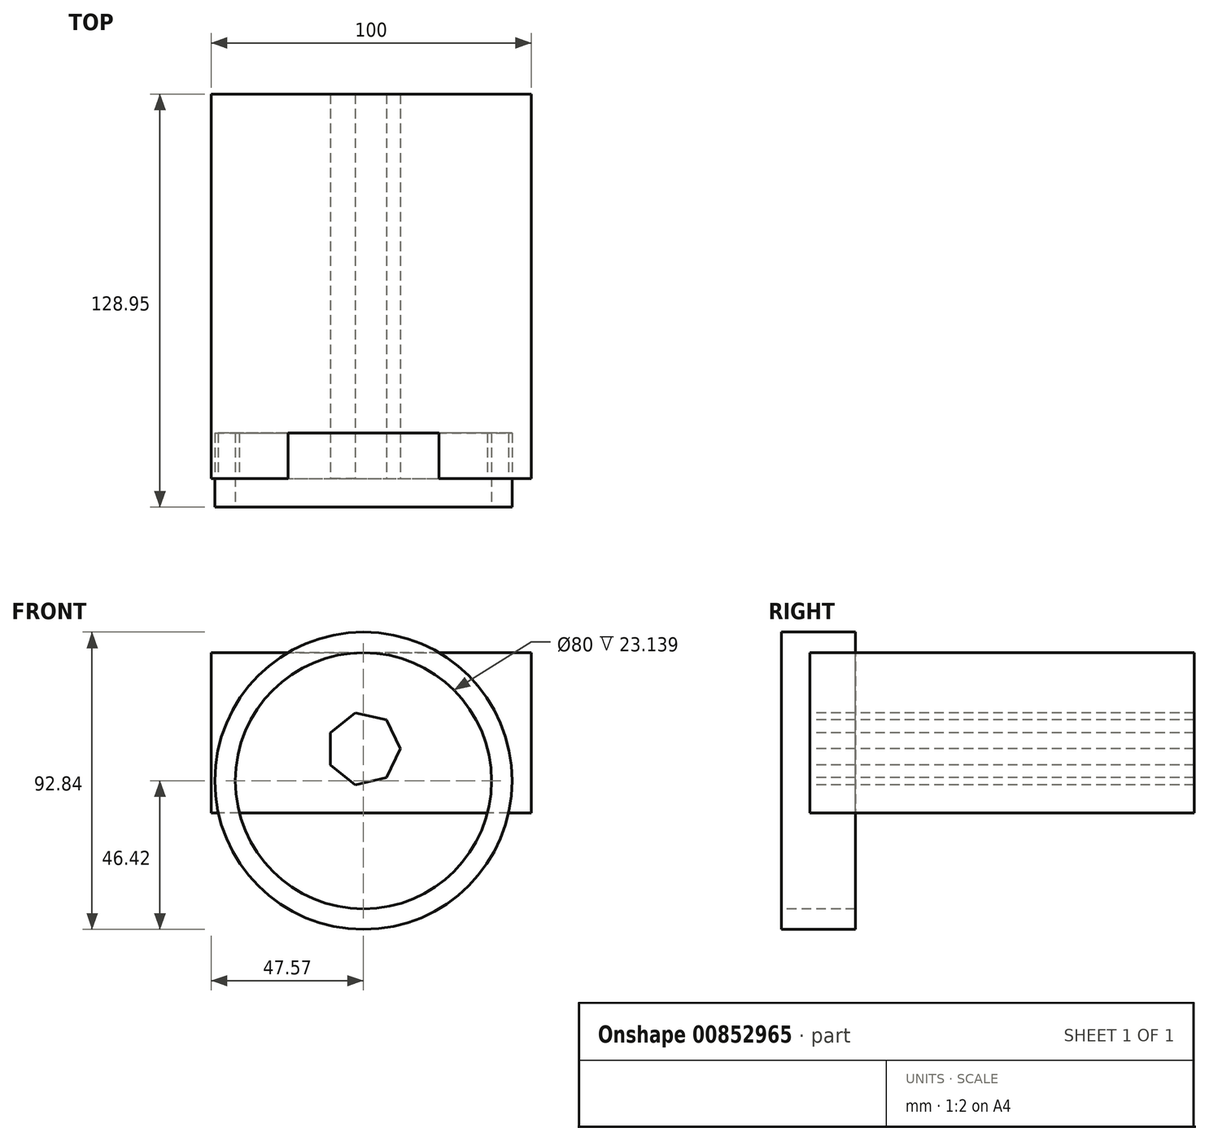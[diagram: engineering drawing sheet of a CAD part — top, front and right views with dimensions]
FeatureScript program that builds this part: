
annotation { "Feature Type Name" : "Feature", "Feature Type Description" : "" }
export const myFeature = defineFeature(function(context is Context, id is Id, definition is map)
    precondition{}
    {
        {
            var Q0;
            Q0=qCreatedBy(makeId("Top.planeOp"),FACE);
            var sketch = newSketch(context, id + "F0", { "sketchPlane" : qUnion([Q0])});
            skLineSegment(sketch, "E0.bottom", {"start": v(-47.57, 87.82) * mm, "end": v(52.43, 87.82) * mm});
            skLineSegment(sketch, "E0.top", {"start": v(-47.57, -32.18) * mm, "end": v(52.43, -32.18) * mm});
            skLineSegment(sketch, "E0.left", {"start": v(-47.57, 87.82) * mm, "end": v(-47.57, -32.18) * mm});
            skLineSegment(sketch, "E0.right", {"start": v(52.43, 87.82) * mm, "end": v(52.43, -32.18) * mm});
            skSolve(sketch);
        }
        {
            var Q0;
            Q0=makeQuery(id+"F0.imprint","IMPRINT",FACE,{"disambiguationData":[TD([[makeQuery(id+"F0.imprint","IMPRINT",EDGE,{"derivedFrom":sQuery(id+"F0.wireOp",EDGE,"E0.bottom")}),-1.0]])]});
            extrude(context, id + "F1", {"entities" : qUnion([Q0]), "depth" : 50 * mm, "offsetDistance" : 25 * mm});
        }
        {
            var Q0;
            Q0=makeQuery(id+"F1.opExtrude","SWEPT_FACE",FACE,{"disambiguationData":[OSD([sQuery(id+"F0.wireOp",EDGE,"E0.top")])]});
            var sketch = newSketch(context, id + "F2", { "sketchPlane" : qUnion([Q0])});
            skCircle(sketch, "E1.cCircle", {"center": v(0, 20) * mm, "radius": 10.38 * mm, "construction": true});
            skLineSegment(sketch, "E1.0", {"start": v(-2.56, 31.23) * mm, "end": v(7.18, 29) * mm});
            skLineSegment(sketch, "E1.1", {"start": v(7.18, 29) * mm, "end": v(11.52, 20) * mm});
            skLineSegment(sketch, "E1.2", {"start": v(11.52, 20) * mm, "end": v(7.18, 11) * mm});
            skLineSegment(sketch, "E1.3", {"start": v(7.18, 11) * mm, "end": v(-2.56, 8.77) * mm});
            skLineSegment(sketch, "E1.4", {"start": v(-2.56, 8.77) * mm, "end": v(-10.38, 15) * mm});
            skLineSegment(sketch, "E1.5", {"start": v(-10.38, 15) * mm, "end": v(-10.38, 25) * mm});
            skLineSegment(sketch, "E1.6", {"start": v(-10.38, 25) * mm, "end": v(-2.56, 31.23) * mm});
            skPoint(sketch, "E1.0.midPoint", {"position": v(2.31, 30.12) * mm});
            skSolve(sketch);
        }
        {
            var Q0;
            Q0=makeQuery(id+"F2.imprint","IMPRINT",FACE,{"disambiguationData":[TD([[makeQuery(id+"F2.imprint","IMPRINT",EDGE,{"derivedFrom":sQuery(id+"F2.wireOp",EDGE,"E1.0")}),-1.0]])]});
            var Q1;
            {var subQ1=sQuery(id+"F2.wireOp",EDGE,"E1.5");Q1=makeQuery(id+"F2.imprint","IMPRINT",FACE,{"disambiguationData":[TD([[makeQuery(id+"F2.imprint","IMPRINT",EDGE,{"derivedFrom":subQ1}),-1.0]])]});}
            extrude(context, id + "F3", {"entities" : qUnion([Q0, Q1]), "operationType" : NewBodyOperationType.REMOVE, "endBound" : BoundingType.THROUGH_ALL, "oppositeDirection" : true, "depth" : 25 * mm, "offsetDistance" : 25 * mm});
        }
        {
            var Q0;
            Q0=qCreatedBy(makeId("Right.planeOp"),FACE);
            var sketch = newSketch(context, id + "F4", { "sketchPlane" : qUnion([Q0])});
            skLineSegment(sketch, "E2.bottom", {"start": v(-41.13, 56.42) * mm, "end": v(-17.99, 56.42) * mm});
            skLineSegment(sketch, "E2.top", {"start": v(-41.13, 50) * mm, "end": v(-17.99, 50) * mm});
            skLineSegment(sketch, "E2.left", {"start": v(-41.13, 56.42) * mm, "end": v(-41.13, 50) * mm});
            skLineSegment(sketch, "E2.right", {"start": v(-17.99, 56.42) * mm, "end": v(-17.99, 50) * mm});
            skLineSegment(sketch, "E3", {"start": v(-65.65, 10) * mm, "end": v(-43.96, 10) * mm});
            skSolve(sketch);
        }
        {
            var Q0;
            Q0=makeQuery(id+"F4.imprint","IMPRINT",FACE,{"disambiguationData":[TD([[makeQuery(id+"F4.imprint","IMPRINT",EDGE,{"derivedFrom":sQuery(id+"F4.wireOp",EDGE,"E2.bottom")}),-1.0]])]});
            var Q1;
            Q1=sQuery(id+"F4.wireOp",EDGE,"E3");
            revolve(context, id + "F5", {"surfaceOperationType" : NewSurfaceOperationType.NEW, "entities" : qUnion([Q0]), "axis" : qUnion([Q1]), "revolveType" : RevolveType.FULL});
        }
        {
            var Q0;
            Q0=makeQuery(id+"F5.opRevolve","SWEPT_BODY",BODY,{"disambiguationData":[OSD([sQuery(id+"F4.wireOp",EDGE,"E2.bottom"),sQuery(id+"F4.wireOp",EDGE,"E2.top"),sQuery(id+"F4.wireOp",EDGE,"E2.left"),sQuery(id+"F4.wireOp",EDGE,"E2.right")])]});
            var Q1;
            Q1=makeQuery(id+"F1.opExtrude","SWEPT_BODY",BODY,{"disambiguationData":[OSD([sQuery(id+"F0.wireOp",EDGE,"E0.bottom"),sQuery(id+"F0.wireOp",EDGE,"E0.top"),sQuery(id+"F0.wireOp",EDGE,"E0.left"),sQuery(id+"F0.wireOp",EDGE,"E0.right")])]});
            booleanBodies(context, id + "F6", {"operationType" : BooleanOperationType.SUBTRACTION, "tools" : qUnion([Q0]), "targets" : qUnion([Q1]), "keepTools" : true});
        }
    });
